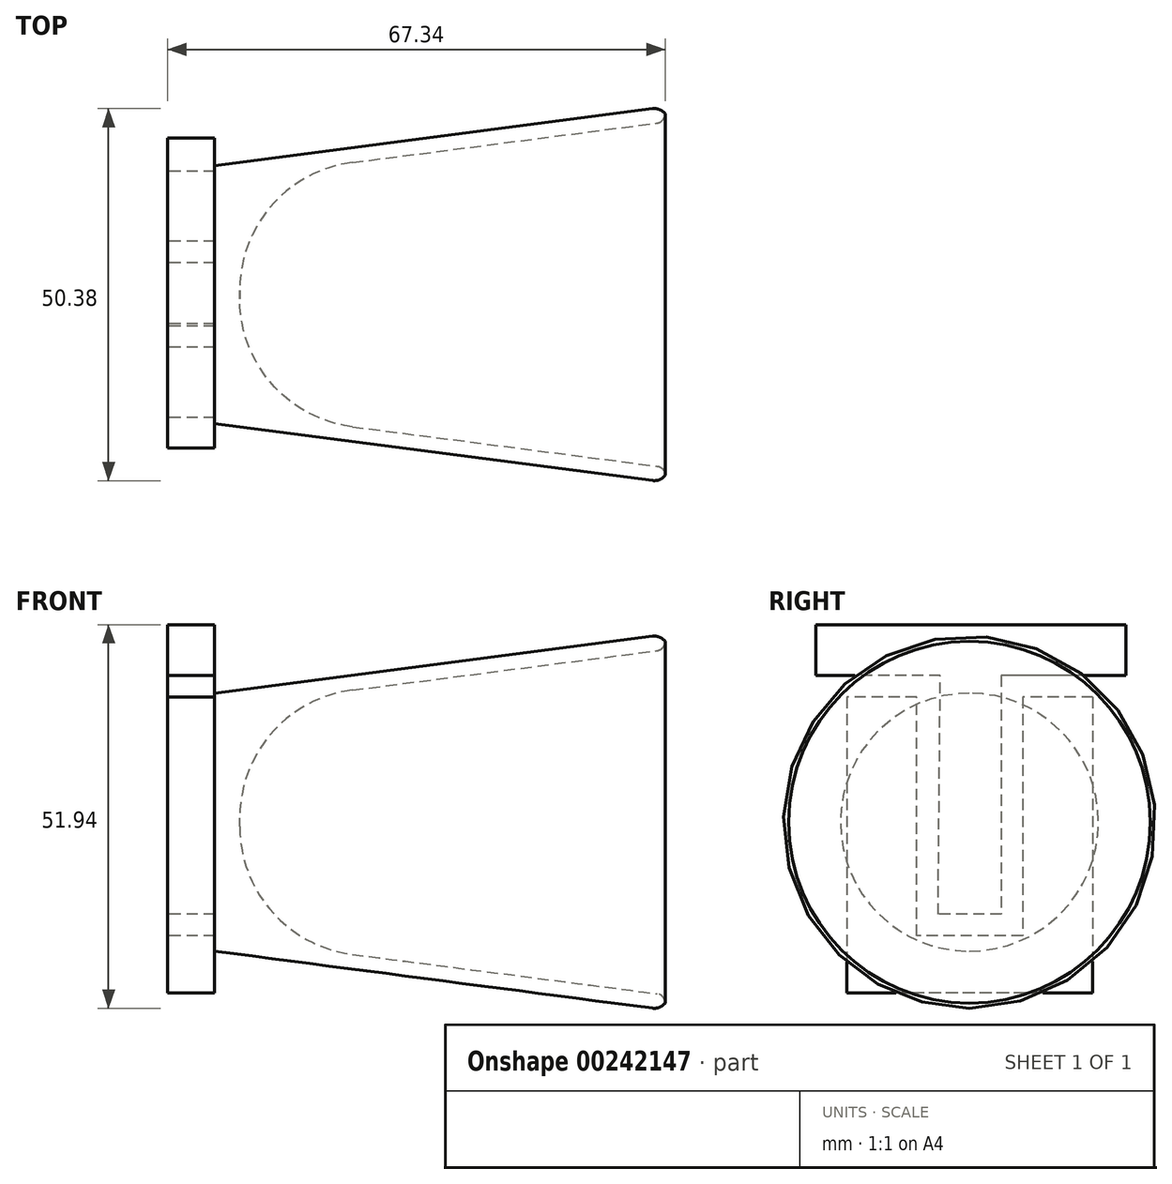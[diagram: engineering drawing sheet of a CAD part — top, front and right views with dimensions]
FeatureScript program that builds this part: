
annotation { "Feature Type Name" : "Feature", "Feature Type Description" : "" }
export const myFeature = defineFeature(function(context is Context, id is Id, definition is map)
    precondition{}
    {
        {
            var Q0;
            Q0=qCreatedBy(makeId("Front.planeOp"),FACE);
            var sketch = newSketch(context, id + "F0", { "sketchPlane" : qUnion([Q0])});
            skLineSegment(sketch, "E0", {"start": v(0, 15.48) * mm, "end": v(0, 17.46) * mm});
            skLineSegment(sketch, "E1", {"start": v(0, 0) * mm, "end": v(60.33, 0) * mm});
            skLineSegment(sketch, "E2", {"start": v(61, 23.37) * mm, "end": v(0, 15.48) * mm});
            skLineSegment(sketch, "E3", {"start": v(0, 15.48) * mm, "end": v(0, 0) * mm});
            skLineSegment(sketch, "E4", {"start": v(3.4, 15.92) * mm, "end": v(3.4, 0) * mm});
            skLineSegment(sketch, "E5", {"start": v(0, 17.46) * mm, "end": v(61, 25.4) * mm});
            skLineSegment(sketch, "E6", {"start": v(61, 25.4) * mm, "end": v(61, 23.37) * mm});
            skSolve(sketch);
        }
        {
            var Q0;
            Q0 = qSketchRegion(id + "F0", true);
            var Q1;
            Q1=sQuery(id+"F0.wireOp",EDGE,"E1");
            revolve(context, id + "F1", {"entities" : qUnion([Q0]), "axis" : qUnion([Q1]), "revolveType" : RevolveType.FULL});
        }
        {
            var Q0;
            Q0=makeQuery(id+"F1.opRevolve","SWEPT_EDGE",EDGE,{"disambiguationData":[OSD([sQuery(id+"F0.wireOp",EDGE,"E2"),sQuery(id+"F0.wireOp",EDGE,"E4")])]});
            fillet(context, id + "F2", {"entities" : qUnion([Q0]), "radius" : 17.46 * mm, "tangentPropagation" : true, "allowEdgeOverflow" : false});
        }
        {
            var Q0;
            Q0=makeQuery(id+"F1.opRevolve","SWEPT_EDGE",EDGE,{"disambiguationData":[OSD([sQuery(id+"F0.wireOp",EDGE,"E2"),sQuery(id+"F0.wireOp",EDGE,"E6")])]});
            fillet(context, id + "F3", {"entities" : qUnion([Q0]), "radius" : 1.27 * mm, "tangentPropagation" : true, "allowEdgeOverflow" : false});
        }
        {
            var Q0;
            Q0=makeQuery(id+"F1.opRevolve","SWEPT_EDGE",EDGE,{"disambiguationData":[OSD([sQuery(id+"F0.wireOp",EDGE,"E5"),sQuery(id+"F0.wireOp",EDGE,"E6")])]});
            fillet(context, id + "F4", {"entities" : qUnion([Q0]), "radius" : 1.9 * mm, "tangentPropagation" : true, "allowEdgeOverflow" : false});
        }
        {
            var Q0;
            Q0=qCreatedBy(makeId("Right.planeOp"),FACE);
            cPlane(context, id + "F5", {"entities" : qUnion([Q0]), "cplaneType" : CPlaneType.OFFSET, "offset" : 6.35 * mm, "oppositeDirection" : true, "width" : 152.4 * mm, "height" : 152.4 * mm});
        }
        {
            var Q0;
            Q0=qCreatedBy(id+"F5.planeOp",FACE);
            var sketch = newSketch(context, id + "F6", { "sketchPlane" : qUnion([Q0])});
            skLineSegment(sketch, "E7", {"start": v(16.69, -23.14) * mm, "end": v(-16.61, -23.14) * mm});
            skLineSegment(sketch, "E8", {"start": v(-20.8, 26.75) * mm, "end": v(21.21, 26.75) * mm});
            skLineSegment(sketch, "E9", {"start": v(21.21, 19.85) * mm, "end": v(4.31, 19.85) * mm});
            skLineSegment(sketch, "E10", {"start": v(4.31, 19.85) * mm, "end": v(4.31, -12.47) * mm});
            skLineSegment(sketch, "E11", {"start": v(4.31, -12.47) * mm, "end": v(-4.24, -12.47) * mm});
            skLineSegment(sketch, "E12", {"start": v(-4.24, -12.47) * mm, "end": v(-3.96, 19.85) * mm});
            skLineSegment(sketch, "E13", {"start": v(-3.96, 19.85) * mm, "end": v(-20.8, 19.85) * mm});
            skLineSegment(sketch, "E14", {"start": v(16.69, 16.95) * mm, "end": v(7.2, 16.95) * mm});
            skLineSegment(sketch, "E15", {"start": v(7.2, 16.95) * mm, "end": v(7.2, -15.37) * mm});
            skLineSegment(sketch, "E16", {"start": v(7.2, -15.37) * mm, "end": v(-7.14, -15.37) * mm});
            skLineSegment(sketch, "E17", {"start": v(-7.14, -15.37) * mm, "end": v(-7.14, 16.95) * mm});
            skLineSegment(sketch, "E18", {"start": v(-7.14, 16.95) * mm, "end": v(-16.61, 16.95) * mm});
            skLineSegment(sketch, "E19", {"start": v(16.69, 16.95) * mm, "end": v(16.69, -23.14) * mm});
            skLineSegment(sketch, "E20", {"start": v(21.21, 19.85) * mm, "end": v(21.21, 26.75) * mm});
            skLineSegment(sketch, "E21", {"start": v(-16.61, 16.95) * mm, "end": v(-16.61, -23.14) * mm});
            skLineSegment(sketch, "E22", {"start": v(-20.8, 19.85) * mm, "end": v(-20.8, 26.75) * mm});
            skSolve(sketch);
        }
        {
            var Q0;
            {var subQ1=sQuery(id+"F6.wireOp",EDGE,"E7");Q0=makeQuery(id+"F6.imprint","IMPRINT",FACE,{"disambiguationData":[TD([[makeQuery(id+"F6.imprint","IMPRINT",EDGE,{"derivedFrom":subQ1}),-1.0]])]});}
            var Q1;
            Q1=makeQuery(id+"F6.imprint","IMPRINT",FACE,{"disambiguationData":[TD([[makeQuery(id+"F6.imprint","IMPRINT",EDGE,{"derivedFrom":sQuery(id+"F6.wireOp",EDGE,"E8")}),-1.0]])]});
            extrude(context, id + "F7", {"entities" : qUnion([Q0, Q1]), "depth" : 6.35 * mm});
        }
    });
